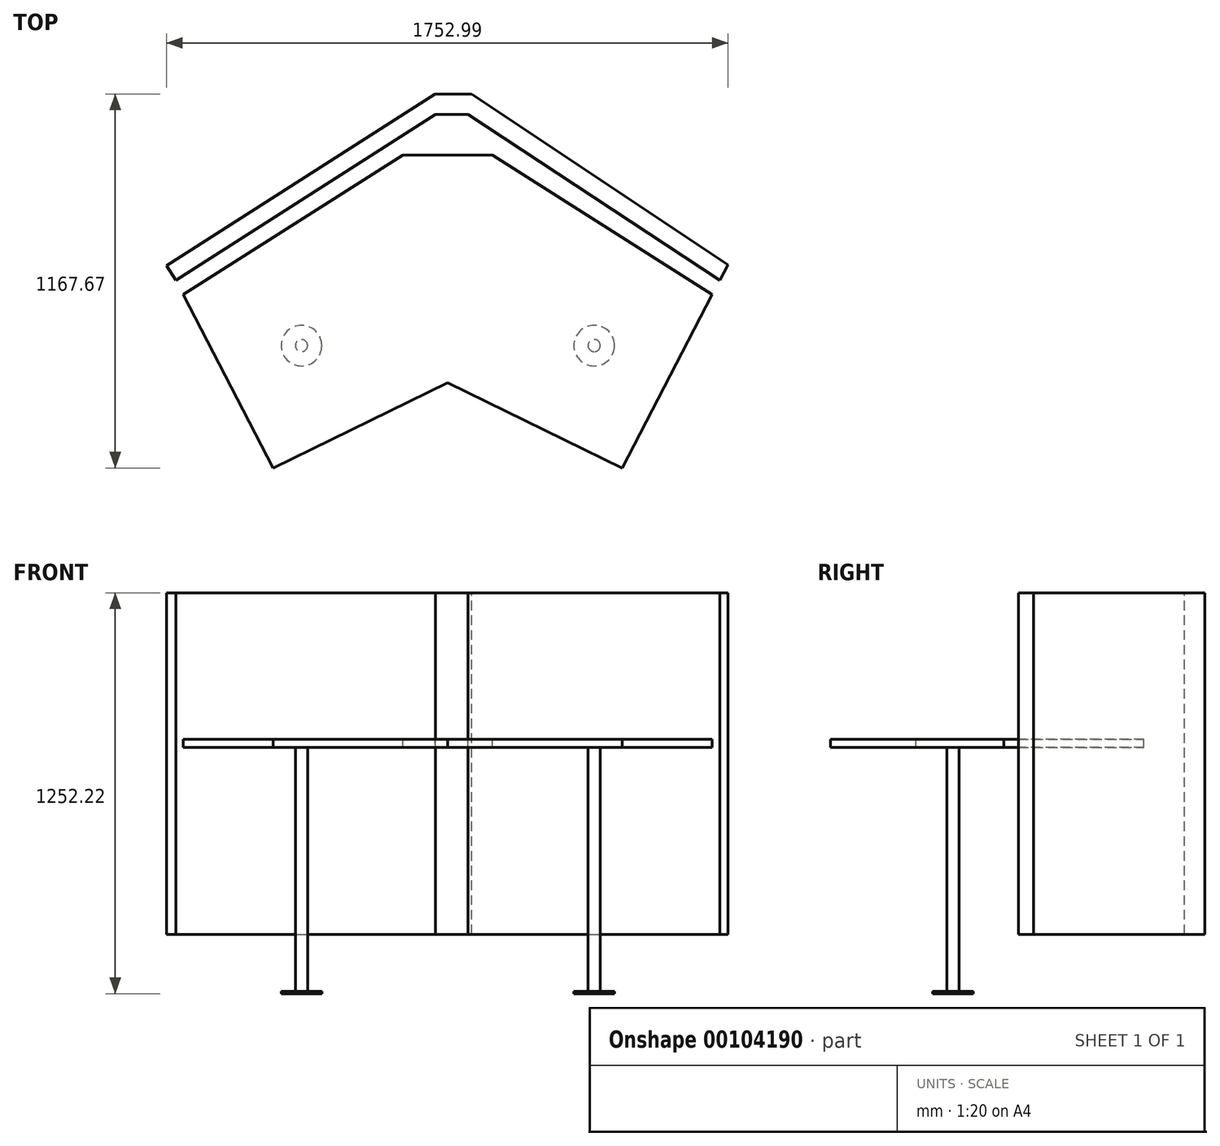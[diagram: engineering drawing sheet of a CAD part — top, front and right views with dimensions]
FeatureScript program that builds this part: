
annotation { "Feature Type Name" : "Feature", "Feature Type Description" : "" }
export const myFeature = defineFeature(function(context is Context, id is Id, definition is map)
    precondition{}
    {
        {
            var Q0;
            Q0=qCreatedBy(makeId("Top.planeOp"),FACE);
            var sketch = newSketch(context, id + "F0", { "sketchPlane" : qUnion([Q0])});
            skLineSegment(sketch, "E0", {"start": v(-139.7, 0) * mm, "end": v(139.7, 0) * mm});
            skPoint(sketch, "E1", {"position": v(0, 0) * mm});
            skLineSegment(sketch, "E2", {"start": v(139.7, 0) * mm, "end": v(825.5, -436.26) * mm});
            skLineSegment(sketch, "E3", {"start": v(825.5, -436.26) * mm, "end": v(544.73, -977.35) * mm});
            skLineSegment(sketch, "E4", {"start": v(544.73, -977.35) * mm, "end": v(0, -711.2) * mm});
            skLineSegment(sketch, "E5", {"start": v(0, -711.2) * mm, "end": v(-544.73, -977.35) * mm});
            skLineSegment(sketch, "E6", {"start": v(-544.73, -977.35) * mm, "end": v(-825.5, -436.26) * mm});
            skLineSegment(sketch, "E7", {"start": v(-825.5, -436.26) * mm, "end": v(-139.7, 0) * mm});
            skSolve(sketch);
        }
        {
            var Q0;
            Q0=qSketchRegion(id+"F0",true);
            extrude(context, id + "F1", {"entities" : qUnion([Q0]), "oppositeDirection" : true, "depth" : 25.4 * mm});
        }
        {
            var Q0;
            Q0=makeQuery(id+"F1.opExtrude","CAP_FACE",FACE,{"disambiguationData":[OSD([sQuery(id+"F0.wireOp",EDGE,"E0"),sQuery(id+"F0.wireOp",EDGE,"E2"),sQuery(id+"F0.wireOp",EDGE,"E3"),sQuery(id+"F0.wireOp",EDGE,"E4"),sQuery(id+"F0.wireOp",EDGE,"E5"),sQuery(id+"F0.wireOp",EDGE,"E6"),sQuery(id+"F0.wireOp",EDGE,"E7")])],"isStart":false});
            var sketch = newSketch(context, id + "F2", { "sketchPlane" : qUnion([Q0])});
            skCircle(sketch, "E8", {"center": v(-456.87, 595.19) * mm, "radius": 19.05 * mm});
            skCircle(sketch, "E9", {"center": v(456.87, 595.19) * mm, "radius": 19.05 * mm});
            skSolve(sketch);
        }
        {
            var Q0;
            Q0 = qSketchRegion(id + "F2", true);
            extrude(context, id + "F3", {"entities" : qUnion([Q0]), "operationType" : NewBodyOperationType.ADD, "depth" : 762 * mm});
        }
        {
            var Q0;
            Q0=makeQuery(id+"F3.opExtrude","CAP_FACE",FACE,{"disambiguationData":[OSD([sQuery(id+"F2.wireOp",EDGE,"E8")])],"isStart":false});
            var sketch = newSketch(context, id + "F4", { "sketchPlane" : qUnion([Q0])});
            skCircle(sketch, "E10", {"center": v(-456.87, 595.19) * mm, "radius": 63.5 * mm});
            skCircle(sketch, "E11", {"center": v(456.87, 595.19) * mm, "radius": 63.5 * mm});
            skSolve(sketch);
        }
        {
            var Q0;
            Q0 = qSketchRegion(id + "F4", true);
            extrude(context, id + "F5", {"entities" : qUnion([Q0]), "operationType" : NewBodyOperationType.ADD, "depth" : 7.62 * mm});
        }
        {
            var Q0;
            Q0=qCreatedBy(makeId("Top.planeOp"),FACE);
            var sketch = newSketch(context, id + "F6", { "sketchPlane" : qUnion([Q0])});
            skLineSegment(sketch, "E12", {"start": v(-848.99, -391) * mm, "end": v(-38.1, 127) * mm});
            skLineSegment(sketch, "E13", {"start": v(-38.1, 127) * mm, "end": v(63.5, 127) * mm});
            skLineSegment(sketch, "E14", {"start": v(63.5, 127) * mm, "end": v(848.99, -391) * mm});
            skLineSegment(sketch, "E15", {"start": v(-848.99, -391) * mm, "end": v(-878.35, -345.03) * mm});
            skLineSegment(sketch, "E16", {"start": v(-878.35, -345.03) * mm, "end": v(-40.28, 190.32) * mm});
            skLineSegment(sketch, "E17", {"start": v(-40.28, 190.32) * mm, "end": v(74.93, 190.32) * mm});
            skLineSegment(sketch, "E18", {"start": v(74.93, 190.32) * mm, "end": v(874.64, -343.52) * mm});
            skLineSegment(sketch, "E19", {"start": v(874.64, -343.52) * mm, "end": v(848.99, -391) * mm});
            skSolve(sketch);
        }
        {
            var Q0;
            Q0 = qSketchRegion(id + "F6", true);
            extrude(context, id + "F7", {"entities" : qUnion([Q0]), "oppositeDirection" : true, "depth" : 609.6 * mm});
        }
        {
            var Q0;
            Q0 = qSketchRegion(id + "F6", true);
            extrude(context, id + "F8", {"entities" : qUnion([Q0]), "operationType" : NewBodyOperationType.ADD, "depth" : 457.2 * mm});
        }
    });
